# Revit family: CLighting-Luminii-Leto_11_P_UD_ADJ
name_source: partatom
category: Lighting Fixtures
units: mm (PartAtom-declared; Revit-internal decimal feet)

## family parameters
Cut with Voids When Loaded = No
Host = Face
Light Source = Yes
OmniClass Number = 23.80.70.11.14.17
OmniClass Title = Direct/Indirect
Part Type = Normal
Room Calculation Point = No
Round Connector Dimension = Use Diameter
Shared = Yes

## types (1)
- Leto 11 P UD ADJ
    Apparent Load = 6 VA
    Assembly Code = D5020200
    CCT = 3500K
    Canopy Finish = Metal - Luminii - Silver Anodized Aluminum
    Color Filter = 16777215
    Constraints = 1
    Control Type = Consult Manufacturer Website for more Information
    Control Zone = Consult Manufacturer Website for more Information
    Current Amps = 50 A
    Default Elevation = 0"
    Depth = 4 15/16"
    Description = Adjustable pendant cylinder
    Dimming Lamp Color Temperature Shift = <None>
    Dimming Type = Consult Manufacturer Website for more Information
    Environment = Indoor
    Finish = Metal - Luminii - Silver Anodized Aluminum
    Frequency = 60 Hz
    Has Battery Backup = No
    Has Dimming = Yes
    Housing Protection Rating = Consult Manufacturer Website for more Information
    Initial Color Comments = Perfomance based on 3500K Photometric Web File
    Keynote = 26 51 00
    Lamp = LED
    Lamp Life = 1
    Lens Material = Plastic - Luminii - Frosted Lens
    Load Classification = Lighting
    Luminaire Type = Uplight and Downlight Pendant LED Light
    Manufacturer = Luminii
    Model = 892
    Mounting Method = Pendant Mount
    Number of Poles = 1
    Operating Temperature = Consult Manufacturer Website for more Information
    Phase = 1
    Photometric Web File = 892-A90-66060-35-0707-00.IES
    Power Factor = 1
    Power Source Type = Driver
    Product Page URL = https://www.luminii.com
    Tilt Angle = -90.00°
    URL = https://www.luminii.com
    Version = 2020 - v1.0a
    Voltage = 120 V
    Voltage Comments = 120V | 277V | 347V
    Warranty URL = https://www.luminii.com
    Wattage Comments = 12.2W
    Width = 4 15/16"

## geometry (parser evidence)
native form markers: Sweep x12
no freeform markers — native parametric forms only
